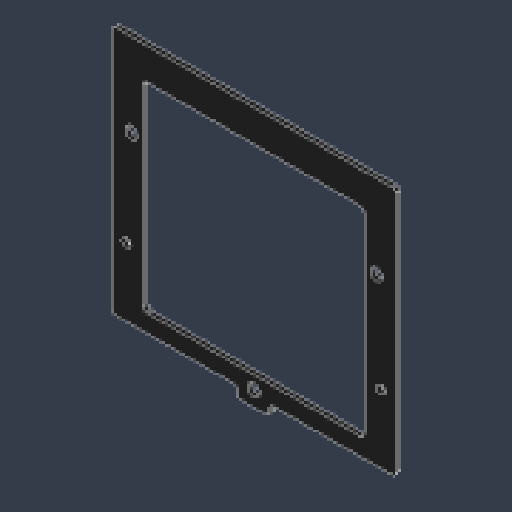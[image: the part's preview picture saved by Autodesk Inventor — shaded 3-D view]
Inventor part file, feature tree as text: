
AUTODESK INVENTOR PART (.ipt)
format: ipt  version: 2023.4 (Build 274418000, 418)  size: 229,888 bytes
history: native  units: mm
features: sketch x8, extrude x7, hole x1, fillet x1
ambient origin geometry x8: Origin, YZ Plane, XZ Plane, XY Plane, X Axis, Y Axis, Z Axis, Center Point
bodies: Solid1 (feature_tree)
feature tree (17):
  extrude  "Extrusion1"  Depth=65.0mm
  hole  "Hole1"  [1 undecoded]
  extrude  "Extrusion2"  Depth=9.0mm
  extrude  "Extrusion3"  TaperAngle=45.0deg  [1 undecoded]
  extrude  "Extrusion4"  Depth=8.0mm
  extrude  "Extrusion5"  Depth=4.0mm
  extrude  "Extrusion6"  Depth=1.3mm
  extrude  "Extrusion7"  Depth=1.0mm
  fillet  "Fillet1"  Radius=9.0mm
  sketch  "Sketch1"  dims[d0=80.0mm d1=65.0mm]
  sketch  "Sketch2"  dims[d2=19.0mm d3=45.0deg]
  sketch  "Sketch4"  dims[d4=9.0mm d5=3.5mm]
  sketch  "Sketch5"  dims[d6=6.0mm d7=45.0deg]
  sketch  "Sketch6"  dims[d8=8.0mm d9=8.0mm]
  sketch  "Sketch7"  dims[d10=12.0mm d11=4.0mm]
  sketch  "Sketch8"  dims[d12=1.3mm d13=0.0mm d14=71.4mm]
  sketch  "Sketch9"  dims[d15=22.7mm d16=2.5mm d17=6.0mm d18=40.0mm d19=25.5mm d20=90.0deg d21=8.0mm d22=20.594885mm d23=3.2mm d24=9.0mm d25=0.4mm d26=6.8mm d27=0.0mm d28=3.4mm d29=68.8mm d30=27.4mm d31=18.0mm d32=0.4mm d33=0.0mm d34=0.0mm d35=0.0mm d36=9.0mm d37=9.0mm d38=9.0mm d39=5.0mm d40=10.0mm d41=0.0mm d42=51.0mm d43=8.0mm d44=5.0mm d45=5.0mm d46=0.0mm d47=0.0mm d48=0.0mm d49=0.0mm d50=1.0mm]
note: 2 required parameter values undecoded (feature->parameter linkage not recoverable at this tier; creation-order binding heuristic only, values carry confidence <= 0.55)
